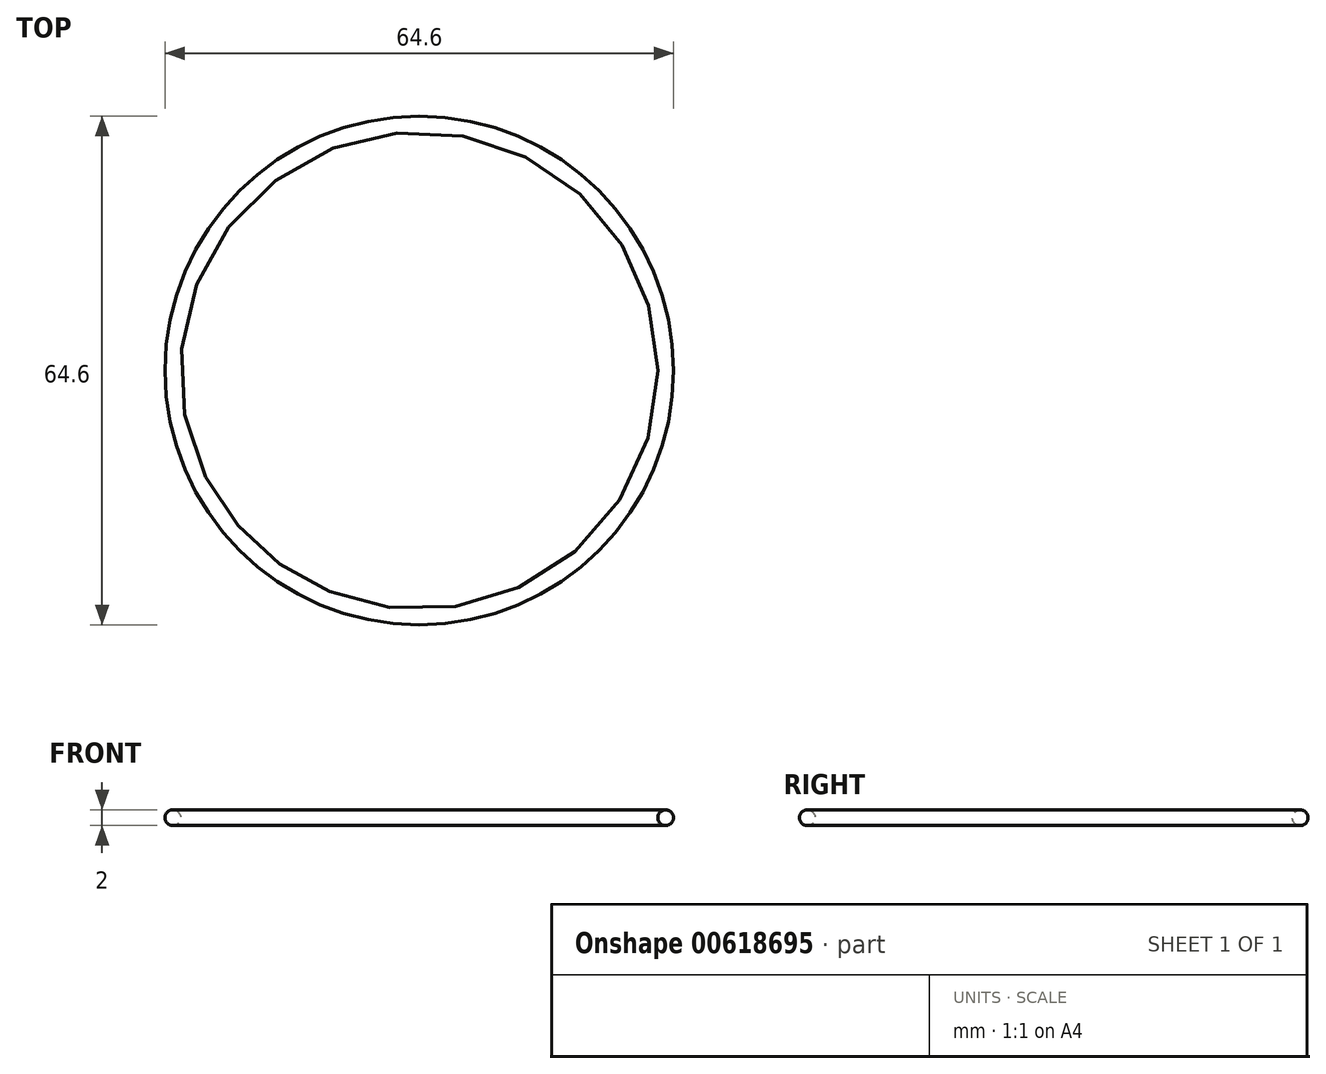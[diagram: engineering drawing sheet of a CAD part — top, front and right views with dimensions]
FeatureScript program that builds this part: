
annotation { "Feature Type Name" : "Feature", "Feature Type Description" : "" }
export const myFeature = defineFeature(function(context is Context, id is Id, definition is map)
    precondition{}
    {
        {
            var Q0;
            Q0=qCreatedBy(makeId("Front.planeOp"),FACE);
            var sketch = newSketch(context, id + "F0", { "sketchPlane" : qUnion([Q0])});
            skCircle(sketch, "E0", {"center": v(-31.3, 0) * mm, "radius": 1 * mm});
            skSolve(sketch);
        }
        {
            var Q0;
            Q0=qCreatedBy(makeId("Front.planeOp"),FACE);
            var sketch = newSketch(context, id + "F1", { "sketchPlane" : qUnion([Q0])});
            skLineSegment(sketch, "E1", {"start": v(0, 27.83) * mm, "end": v(0, -27.34) * mm, "construction": true});
            skSolve(sketch);
        }
        {
            var Q0;
            Q0=makeQuery(id+"F0.imprint","IMPRINT",FACE,{"disambiguationData":[TD([[makeQuery(id+"F0.imprint","IMPRINT",EDGE,{"derivedFrom":sQuery(id+"F0.wireOp",EDGE,"E0")}),1.0]])]});
            var Q1;
            Q1=sQuery(id+"F1.wireOp",EDGE,"E1");
            revolve(context, id + "F2", {"surfaceOperationType" : NewSurfaceOperationType.NEW, "entities" : qUnion([Q0]), "axis" : qUnion([Q1]), "revolveType" : RevolveType.FULL});
        }
    });
